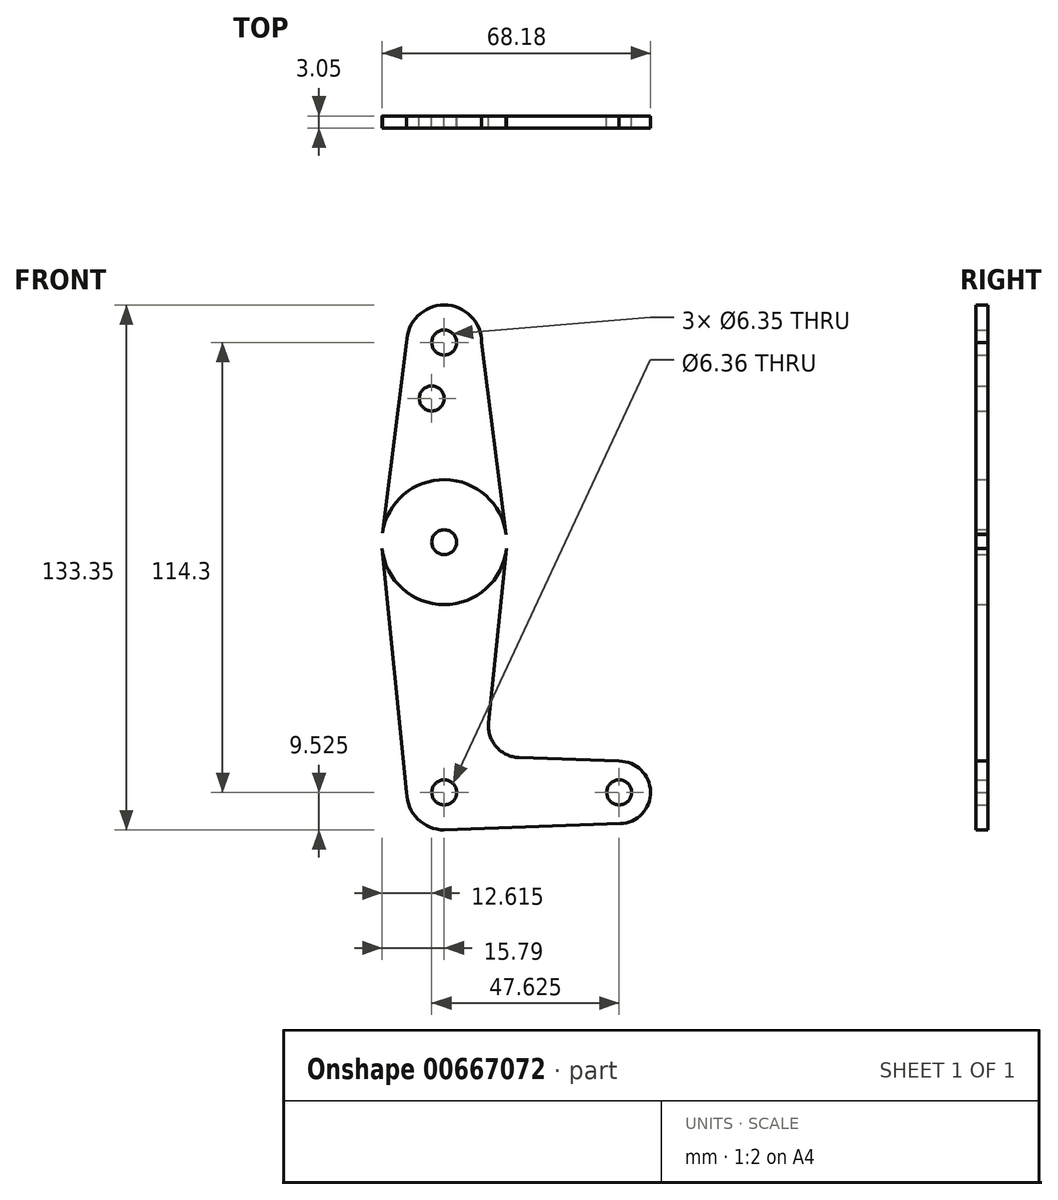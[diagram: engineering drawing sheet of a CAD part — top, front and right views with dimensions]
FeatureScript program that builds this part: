
annotation { "Feature Type Name" : "Feature", "Feature Type Description" : "" }
export const myFeature = defineFeature(function(context is Context, id is Id, definition is map)
    precondition{}
    {
        {
            var Q0;
            Q0=qCreatedBy(makeId("Front.planeOp"),FACE);
            var sketch = newSketch(context, id + "F0", { "sketchPlane" : qUnion([Q0])});
            skLineSegment(sketch, "E0", {"start": v(0, 62.54) * mm, "end": v(0, -51.76) * mm});
            skLineSegment(sketch, "E1", {"start": v(0, -51.76) * mm, "end": v(44.45, -51.76) * mm});
            skCircle(sketch, "E2", {"center": v(0, 62.54) * mm, "radius": 9.53 * mm});
            skCircle(sketch, "E3", {"center": v(0, 11.8) * mm, "radius": 15.88 * mm});
            skCircle(sketch, "E4", {"center": v(44.45, -51.76) * mm, "radius": 7.94 * mm});
            skCircle(sketch, "E5", {"center": v(0, -51.76) * mm, "radius": 9.53 * mm});
            skLineSegment(sketch, "E6", {"start": v(0, -51.76) * mm, "end": v(9.53, -51.76) * mm});
            skLineSegment(sketch, "E7", {"start": v(9.53, 62.54) * mm, "end": v(15.8, 13.45) * mm});
            skLineSegment(sketch, "E8", {"start": v(-9.53, -51.76) * mm, "end": v(-15.8, 10.21) * mm});
            skLineSegment(sketch, "E9", {"start": v(-9.53, 62.54) * mm, "end": v(-15.79, 13.45) * mm});
            skLineSegment(sketch, "E10", {"start": v(0, -61.28) * mm, "end": v(44.73, -59.69) * mm});
            skCircle(sketch, "E11", {"center": v(0, 62.54) * mm, "radius": 3.18 * mm});
            skCircle(sketch, "E12", {"center": v(0, 11.8) * mm, "radius": 3.18 * mm});
            skLineSegment(sketch, "E13", {"start": v(0, 11.8) * mm, "end": v(0, 48.33) * mm});
            skLineSegment(sketch, "E14", {"start": v(0, 48.33) * mm, "end": v(-3.17, 48.33) * mm});
            skCircle(sketch, "E15", {"center": v(-3.17, 48.33) * mm, "radius": 3.17 * mm});
            skCircle(sketch, "E16", {"center": v(0, -51.76) * mm, "radius": 3.18 * mm});
            skArc(sketch, "E17.filletArc", {"start": v(11.3, -34.16) * mm, "mid": v(13.22, -40.18) * mm, "end": v(18.93, -42.9) * mm});
            skCircle(sketch, "E18", {"center": v(44.45, -51.76) * mm, "radius": 3.18 * mm});
            skLineSegment(sketch, "E19", {"start": v(15.8, 10.21) * mm, "end": v(11.3, -34.16) * mm});
            skLineSegment(sketch, "E20", {"start": v(44.45, -43.82) * mm, "end": v(18.93, -42.9) * mm});
            skSolve(sketch);
        }
        {
            var Q0;
            {var subQ0=sQuery(id+"F0.wireOp",EDGE,"E5");var subQ1=sQuery(id+"F0.wireOp",EDGE,"E0");var subQ2=makeQuery(id+"F0.imprint","INTERSECT",VERTEX,{"derivedFrom":[subQ1,subQ0]});Q0=makeQuery(id+"F0.imprint","IMPRINT",FACE,{"disambiguationData":[TD([[makeQuery(id+"F0.imprint","IMPRINT",EDGE,{"disambiguationData":[TD([[subQ2,-1.0]])],"derivedFrom":subQ1}),1.0]])]});}
            var Q1;
            {var subQ1=sQuery(id+"F0.wireOp",EDGE,"E5");var subQ7=sQuery(id+"F0.wireOp",EDGE,"E0");var subQ8=makeQuery(id+"F0.imprint","INTERSECT",VERTEX,{"derivedFrom":[subQ7,subQ1]});Q1=makeQuery(id+"F0.imprint","IMPRINT",FACE,{"disambiguationData":[TD([[makeQuery(id+"F0.imprint","IMPRINT",EDGE,{"disambiguationData":[TD([[subQ8,-1.0]])],"derivedFrom":subQ7}),-1.0]])]});}
            var Q2;
            Q2=makeQuery(id+"F0.imprint","IMPRINT",FACE,{"disambiguationData":[TD([[makeQuery(id+"F0.imprint","IMPRINT",EDGE,{"derivedFrom":sQuery(id+"F0.wireOp",EDGE,"E17.filletArc")}),-1.0]])]});
            var Q3;
            {var subQ3=sQuery(id+"F0.wireOp",EDGE,"E4");var subQ5=sQuery(id+"F0.wireOp",EDGE,"E10");var subQ6=makeQuery(id+"F0.imprint","INTERSECT",VERTEX,{"derivedFrom":[subQ3,subQ5]});Q3=makeQuery(id+"F0.imprint","IMPRINT",FACE,{"disambiguationData":[TD([[makeQuery(id+"F0.imprint","IMPRINT",EDGE,{"disambiguationData":[TD([[subQ6,1.0]])],"derivedFrom":subQ3}),-1.0]])]});}
            var Q4;
            Q4=makeQuery(id+"F0.imprint","IMPRINT",FACE,{"disambiguationData":[TD([[makeQuery(id+"F0.imprint","IMPRINT",EDGE,{"derivedFrom":sQuery(id+"F0.wireOp",EDGE,"E18")}),-1.0]])]});
            var Q5;
            {var subQ5=sQuery(id+"F0.wireOp",EDGE,"E8");Q5=makeQuery(id+"F0.imprint","IMPRINT",FACE,{"disambiguationData":[TD([[makeQuery(id+"F0.imprint","IMPRINT",EDGE,{"derivedFrom":subQ5}),-1.0]])]});}
            var Q6;
            {var subQ2=sQuery(id+"F0.wireOp",EDGE,"E0");var subQ7=sQuery(id+"F0.wireOp",EDGE,"E12");var subQ9=makeQuery(id+"F0.imprint","INTERSECT",VERTEX,{"derivedFrom":[subQ2,subQ7]});Q6=makeQuery(id+"F0.imprint","IMPRINT",FACE,{"disambiguationData":[TD([[makeQuery(id+"F0.imprint","IMPRINT",EDGE,{"disambiguationData":[TD([[subQ9,-1.0]])],"derivedFrom":subQ2}),1.0]])]});}
            var Q7;
            {var subQ2=sQuery(id+"F0.wireOp",EDGE,"E0");var subQ6=sQuery(id+"F0.wireOp",EDGE,"E12");var subQ7=makeQuery(id+"F0.imprint","INTERSECT",VERTEX,{"derivedFrom":[subQ2,subQ6]});Q7=makeQuery(id+"F0.imprint","IMPRINT",FACE,{"disambiguationData":[TD([[makeQuery(id+"F0.imprint","IMPRINT",EDGE,{"disambiguationData":[TD([[subQ7,-1.0]])],"derivedFrom":subQ2}),-1.0]])]});}
            var Q8;
            {var subQ9=sQuery(id+"F0.wireOp",EDGE,"E15");Q8=makeQuery(id+"F0.imprint","IMPRINT",FACE,{"disambiguationData":[TD([[makeQuery(id+"F0.imprint","IMPRINT",EDGE,{"derivedFrom":subQ9}),-1.0]])]});}
            var Q9;
            {var subQ0=sQuery(id+"F0.wireOp",EDGE,"E7");var subQ1=sQuery(id+"F0.wireOp",EDGE,"E2");var subQ2=makeQuery(id+"F0.imprint","INTERSECT",VERTEX,{"derivedFrom":[subQ1,subQ0]});Q9=makeQuery(id+"F0.imprint","IMPRINT",FACE,{"disambiguationData":[TD([[makeQuery(id+"F0.imprint","IMPRINT",EDGE,{"disambiguationData":[TD([[subQ2,1.0]])],"derivedFrom":subQ1}),-1.0]])]});}
            var Q10;
            Q10=makeQuery(id+"F0.imprint","IMPRINT",FACE,{"disambiguationData":[TD([[makeQuery(id+"F0.imprint","IMPRINT",EDGE,{"derivedFrom":sQuery(id+"F0.wireOp",EDGE,"E11")}),-1.0]])]});
            extrude(context, id + "F1", {"entities" : qUnion([Q0, Q1, Q2, Q3, Q4, Q5, Q6, Q7, Q8, Q9, Q10]), "depth" : 3.05 * mm, "offsetDistance" : 25.4 * mm});
        }
    });
